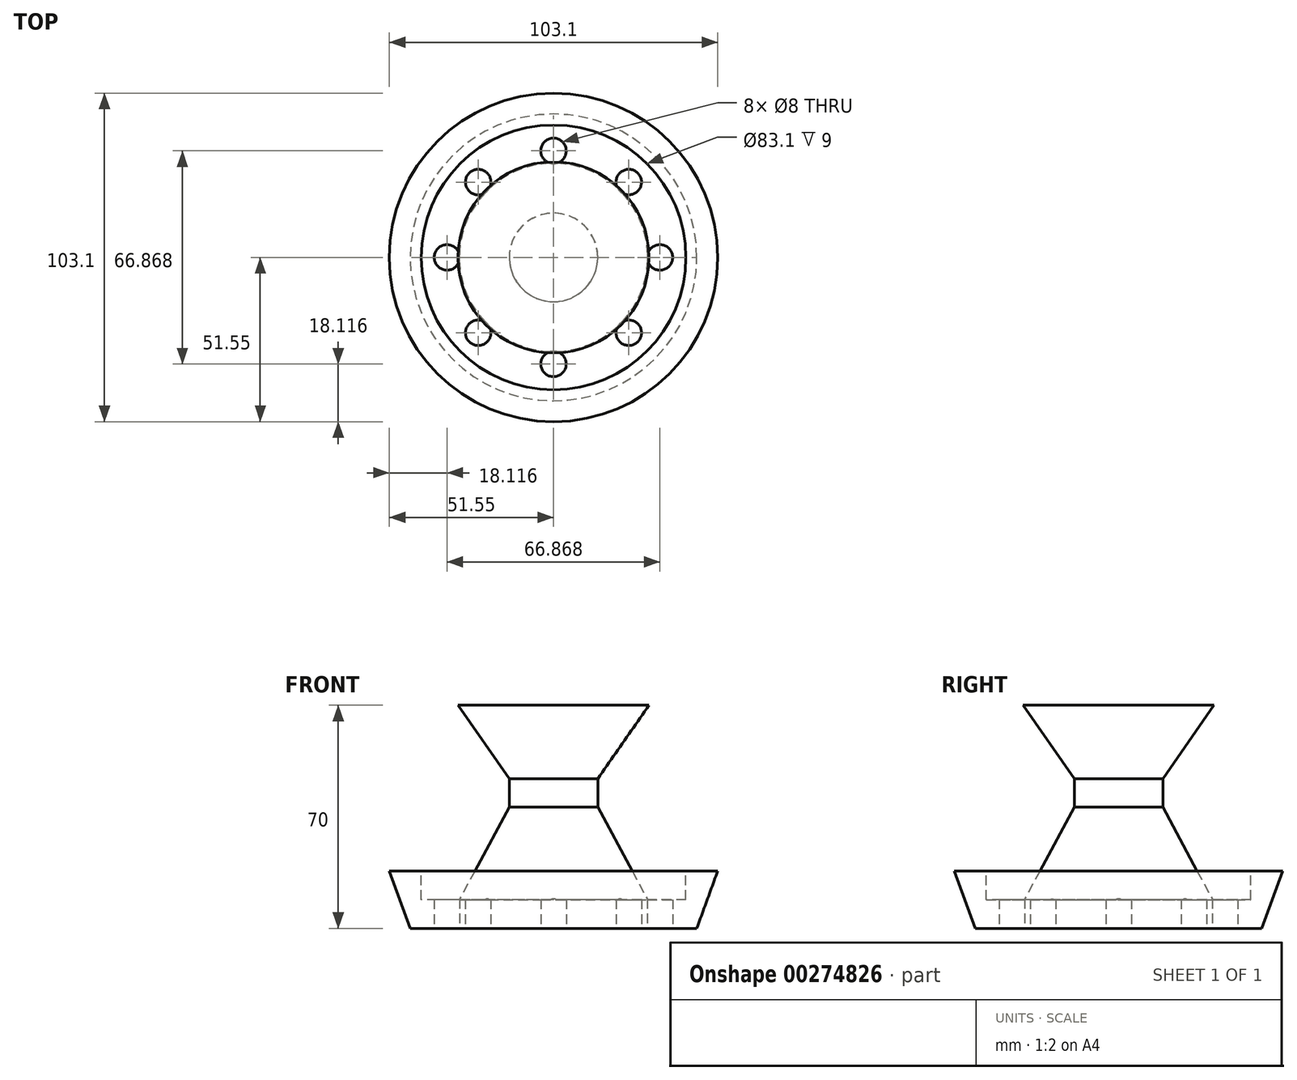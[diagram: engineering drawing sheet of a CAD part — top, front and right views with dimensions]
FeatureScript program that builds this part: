
annotation { "Feature Type Name" : "Feature", "Feature Type Description" : "" }
export const myFeature = defineFeature(function(context is Context, id is Id, definition is map)
    precondition{}
    {
        {
            var Q0;
            Q0=qCreatedBy(makeId("Front.planeOp"),FACE);
            var sketch = newSketch(context, id + "F0", { "sketchPlane" : qUnion([Q0])});
            skLineSegment(sketch, "E0", {"start": v(0, 34.63) * mm, "end": v(0, -35.37) * mm});
            skLineSegment(sketch, "E1", {"start": v(0, -35.37) * mm, "end": v(-45, -35.37) * mm});
            skLineSegment(sketch, "E2", {"start": v(0, 34.63) * mm, "end": v(-30, 34.63) * mm});
            skLineSegment(sketch, "E3", {"start": v(-45, -35.37) * mm, "end": v(-51.55, -17.37) * mm});
            skLineSegment(sketch, "E4", {"start": v(-51.55, -17.37) * mm, "end": v(-41.55, -17.37) * mm});
            skLineSegment(sketch, "E5", {"start": v(-41.55, -17.37) * mm, "end": v(-41.55, -26.37) * mm});
            skLineSegment(sketch, "E6", {"start": v(-41.55, -26.37) * mm, "end": v(-29.55, -26.37) * mm});
            skLineSegment(sketch, "E7", {"start": v(-29.55, -26.37) * mm, "end": v(-13.9, 2.63) * mm});
            skLineSegment(sketch, "E8", {"start": v(-13.9, 2.63) * mm, "end": v(-13.9, 11.63) * mm});
            skLineSegment(sketch, "E9", {"start": v(-13.9, 11.63) * mm, "end": v(-30, 34.63) * mm});
            skSolve(sketch);
        }
        {
            var Q0;
            Q0=makeQuery(id+"F0.imprint","IMPRINT",FACE,{"disambiguationData":[TD([[makeQuery(id+"F0.imprint","IMPRINT",EDGE,{"derivedFrom":sQuery(id+"F0.wireOp",EDGE,"E0")}),-1.0]])]});
            var Q1;
            Q1=sQuery(id+"F0.wireOp",EDGE,"E0");
            revolve(context, id + "F1", {"entities" : qUnion([Q0]), "axis" : qUnion([Q1]), "revolveType" : RevolveType.FULL});
        }
        {
            var Q0;
            Q0=makeQuery(id+"F1.opRevolve","SWEPT_FACE",FACE,{"disambiguationData":[OSD([sQuery(id+"F0.wireOp",EDGE,"E1")])]});
            var sketch = newSketch(context, id + "F2", { "sketchPlane" : qUnion([Q0])});
            skCircle(sketch, "E10", {"center": v(-33.43, 0) * mm, "radius": 4 * mm});
            skCircle(sketch, "E11.1.0", {"center": v(-23.64, -23.64) * mm, "radius": 4 * mm});
            skCircle(sketch, "E11.2.0", {"center": v(0, -33.43) * mm, "radius": 4 * mm});
            skCircle(sketch, "E11.3.0", {"center": v(23.64, -23.64) * mm, "radius": 4 * mm});
            skCircle(sketch, "E11.4.0", {"center": v(33.43, 0) * mm, "radius": 4 * mm});
            skCircle(sketch, "E11.5.0", {"center": v(23.64, 23.64) * mm, "radius": 4 * mm});
            skCircle(sketch, "E11.6.0", {"center": v(0, 33.43) * mm, "radius": 4 * mm});
            skCircle(sketch, "E11.7.0", {"center": v(-23.64, 23.64) * mm, "radius": 4 * mm});
            skPoint(sketch, "E11.center", {"position": v(0, 0) * mm});
            skSolve(sketch);
        }
        {
            var Q0;
            Q0=makeQuery(id+"F2.imprint","IMPRINT",FACE,{"disambiguationData":[TD([[makeQuery(id+"F2.imprint","IMPRINT",EDGE,{"derivedFrom":sQuery(id+"F2.wireOp",EDGE,"E10")}),1.0]])]});
            var Q1;
            Q1=makeQuery(id+"F2.imprint","IMPRINT",FACE,{"disambiguationData":[TD([[makeQuery(id+"F2.imprint","IMPRINT",EDGE,{"derivedFrom":sQuery(id+"F2.wireOp",EDGE,"E11.1.0")}),1.0]])]});
            var Q2;
            Q2=makeQuery(id+"F2.imprint","IMPRINT",FACE,{"disambiguationData":[TD([[makeQuery(id+"F2.imprint","IMPRINT",EDGE,{"derivedFrom":sQuery(id+"F2.wireOp",EDGE,"E11.2.0")}),1.0]])]});
            var Q3;
            Q3=makeQuery(id+"F2.imprint","IMPRINT",FACE,{"disambiguationData":[TD([[makeQuery(id+"F2.imprint","IMPRINT",EDGE,{"derivedFrom":sQuery(id+"F2.wireOp",EDGE,"E11.3.0")}),1.0]])]});
            var Q4;
            Q4=makeQuery(id+"F2.imprint","IMPRINT",FACE,{"disambiguationData":[TD([[makeQuery(id+"F2.imprint","IMPRINT",EDGE,{"derivedFrom":sQuery(id+"F2.wireOp",EDGE,"E11.4.0")}),1.0]])]});
            var Q5;
            Q5=makeQuery(id+"F2.imprint","IMPRINT",FACE,{"disambiguationData":[TD([[makeQuery(id+"F2.imprint","IMPRINT",EDGE,{"derivedFrom":sQuery(id+"F2.wireOp",EDGE,"E11.5.0")}),1.0]])]});
            var Q6;
            Q6=makeQuery(id+"F2.imprint","IMPRINT",FACE,{"disambiguationData":[TD([[makeQuery(id+"F2.imprint","IMPRINT",EDGE,{"derivedFrom":sQuery(id+"F2.wireOp",EDGE,"E11.6.0")}),1.0]])]});
            var Q7;
            Q7=makeQuery(id+"F2.imprint","IMPRINT",FACE,{"disambiguationData":[TD([[makeQuery(id+"F2.imprint","IMPRINT",EDGE,{"derivedFrom":sQuery(id+"F2.wireOp",EDGE,"E11.7.0")}),1.0]])]});
            extrude(context, id + "F3", {"entities" : qUnion([Q0, Q1, Q2, Q3, Q4, Q5, Q6, Q7]), "operationType" : NewBodyOperationType.REMOVE, "endBound" : BoundingType.UP_TO_NEXT, "oppositeDirection" : true, "depth" : 25 * mm});
        }
    });
